# Revit family: 3M_Butterfly Valve_UNIVAL_BWN-0301 - 40-600 mm
name_source: partatom
category: Pipe Accessories
revit_build: Autodesk Revit 2016 (Build: 20150220_1215(x64)
units: mm (PartAtom-declared; Revit-internal decimal feet)

## family parameters
Always vertical = Yes
Cut with Voids When Loaded = No
OmniClass Number = 23.65.55.14.17
OmniClass Title = Adjusting/Controlling Valves for Liquid Services
Part Type = Valve - Breaks Into
Round Connector Dimension = Use Diameter
Shared = No
Work Plane-Based = No

## types (15) — shared parameters
Body Material = Cast iron
Certifications = TSE EAC CE
Connection Type = Wafer
Description = Wafer type butterfly valve
Description TR = Wafer tip kelebek vana
Disc Material = Nickel plated ductile iron
K Coefficient Table = Butterfly Valve Full Open
Loss Method = K Coefficient from Table
Manufacturer = Giacomini Unival
Giacomini Unival
Max. Working Pressure = 11 Bar
Max. Working Temperature = EPDM 120°C (water), NBR 90°C (water and petroleum oil)
Pressure Rating = PN16
Standard No = TS EN 593+A1
URL = http://www.unival.com.tr

## per-type parameters (varying)
- DN100: A=180 mm; B=100 mm; Body_r=73 mm; D=90 mm; DN=100 mm; Disc_r=50 mm  [stored 0.164042 ft]; E=52 mm; EarBottom_h=90 mm; EarEdge_r=25 mm  [stored 0.082021 ft]; Ear_x1=32 mm  [stored 0.104987 ft]; Ear_y1=40 mm  [stored 0.131234 ft]; Eclipse_angle=30.00°; Eclipse_h=86 mm; Eclipse_l=36 mm  [stored 0.11811 ft]; Eclipse_r1=26 mm  [stored 0.0853018 ft]; Eclipse_r2=20 mm  [stored 0.0656168 ft]; Gasket Material=EPDM / NBR; Kv=760; Max Diff. Pressure (Allowed)=3 Bar; Model=BWN-0201X100; Operator Type=M_Handle - Curved : Lever_260mm; Seat Material=EPDM / NBR / VITON / PTFE; Stem_D=35 mm  [stored 0.114829 ft]; Stem_top_h=1 mm  [stored 0.00328084 ft]; T=-10 mm  [stored -0.0328084 ft]
- DN250: A=274 mm; B=200 mm; Body_r=148 mm; D=125 mm; DN=250 mm; Disc_r=125 mm; E=69 mm; EarBottom_h=180 mm; EarEdge_r=32 mm  [stored 0.104987 ft]; Ear_x1=75 mm; Ear_y1=70 mm; Eclipse_angle=30.00°; Eclipse_h=168 mm; Eclipse_l=70 mm; Eclipse_r1=52 mm; Eclipse_r2=40 mm  [stored 0.131234 ft]; Gasket Material=EPDM, NBR; Kv=5050; Max Diff. Pressure (Allowed)=1.5 Bar; Model=BWN-0201X250; Operator Type=M_Handle - Curved : Lever_416mm; Seat Material=EPDM / NBR / VITON / PTFE; Stem_D=46 mm  [stored 0.150919 ft]; Stem_top_h=26 mm  [stored 0.0853018 ft]; T=-10 mm  [stored -0.0328084 ft]
- DN40: A=140 mm; B=64 mm; Body_r=43 mm  [stored 0.141076 ft]; D=90 mm; DN=40 mm; Disc_r=20 mm  [stored 0.0656168 ft]; E=35 mm  [stored 0.114829 ft]; EarBottom_h=54 mm  [stored 0.177165 ft]; EarEdge_r=10 mm  [stored 0.0328084 ft]; Ear_x1=20 mm  [stored 0.0656168 ft]; Ear_y1=22 mm  [stored 0.0721785 ft]; Eclipse_angle=20.00°; Eclipse_h=50 mm  [stored 0.164042 ft]; Eclipse_l=20 mm  [stored 0.0656168 ft]; Eclipse_r1=18 mm  [stored 0.0590551 ft]; Eclipse_r2=14 mm  [stored 0.0459318 ft]; Gasket Material=EPDM, NBR; Kv=49.5; Max Diff. Pressure (Allowed)=3 Bar; Model=BWN-0201X040; Operator Type=M_Handle - Curved : Lever_260mm; Seat Material=EPDM / NBR / VITON / PTFE; Stem_D=23 mm  [stored 0.0754593 ft]; Stem_top_h=1 mm  [stored 0.00328084 ft]; T=-10 mm  [stored -0.0328084 ft]
- DN50: A=140 mm; B=69 mm; Body_r=48 mm  [stored 0.15748 ft]; D=90 mm; DN=50 mm; Disc_r=25 mm  [stored 0.082021 ft]; E=43 mm  [stored 0.141076 ft]; EarBottom_h=60 mm; EarEdge_r=14 mm  [stored 0.0459318 ft]; Ear_x1=20 mm  [stored 0.0656168 ft]; Ear_y1=22 mm  [stored 0.0721785 ft]; Eclipse_angle=30.00°; Eclipse_h=56 mm  [stored 0.183727 ft]; Eclipse_l=22 mm  [stored 0.0721785 ft]; Eclipse_r1=18 mm  [stored 0.0590551 ft]; Eclipse_r2=14 mm  [stored 0.0459318 ft]; Gasket Material=EPDM, NBR; Kv=115; Max Diff. Pressure (Allowed)=3 Bar; Model=BWN-0201X050; Operator Type=M_Handle - Curved : Lever_260mm; Seat Material=EPDM / NBR / VITON / PTFE; Stem_D=29 mm; Stem_top_h=1 mm  [stored 0.00328084 ft]; T=-10 mm  [stored -0.0328084 ft]
- DN65: A=152 mm; B=76 mm; Body_r=56 mm  [stored 0.183727 ft]; D=90 mm; DN=65 mm; Disc_r=33 mm; E=45 mm  [stored 0.147638 ft]; EarBottom_h=70 mm; EarEdge_r=14 mm  [stored 0.0459318 ft]; Ear_x1=20 mm  [stored 0.0656168 ft]; Ear_y1=22 mm  [stored 0.0721785 ft]; Eclipse_angle=30.00°; Eclipse_h=65 mm; Eclipse_l=23 mm  [stored 0.0754593 ft]; Eclipse_r1=18 mm  [stored 0.0590551 ft]; Eclipse_r2=14 mm  [stored 0.0459318 ft]; Gasket Material=EPDM, NBR; Kv=255; Max Diff. Pressure (Allowed)=3 Bar; Model=BWN-0201X065; Operator Type=M_Handle - Curved : Lever_260mm; Seat Material=EPDM / NBR / VITON / PTFE; Stem_D=30 mm  [stored 0.0984252 ft]; Stem_top_h=1 mm  [stored 0.00328084 ft]; T=-10 mm  [stored -0.0328084 ft]
- DN80: A=160 mm; B=85 mm; Body_r=63 mm; D=90 mm; DN=80 mm; Disc_r=40 mm  [stored 0.131234 ft]; E=46 mm  [stored 0.150919 ft]; EarBottom_h=75 mm; EarEdge_r=20 mm  [stored 0.0656168 ft]; Ear_x1=22 mm  [stored 0.0721785 ft]; Ear_y1=22 mm  [stored 0.0721785 ft]; Eclipse_angle=30.00°; Eclipse_h=70 mm; Eclipse_l=27 mm  [stored 0.0885827 ft]; Eclipse_r1=20 mm  [stored 0.0656168 ft]; Eclipse_r2=15 mm  [stored 0.0492126 ft]; Gasket Material=EPDM, NBR; Kv=375; Max Diff. Pressure (Allowed)=3 Bar; Model=BWN-0201X080; Operator Type=M_Handle - Curved : Lever_260mm; Seat Material=EPDM / NBR / VITON / PTFE; Stem_D=31 mm; Stem_top_h=1 mm  [stored 0.00328084 ft]; T=-10 mm  [stored -0.0328084 ft]
- DN125: A=191 mm; B=120 mm; Body_r=86 mm; D=90 mm; DN=125 mm; Disc_r=63 mm; E=56 mm  [stored 0.183727 ft]; EarBottom_h=105 mm; EarEdge_r=28 mm  [stored 0.0918635 ft]; Ear_x1=34 mm; Ear_y1=36 mm  [stored 0.11811 ft]; Eclipse_angle=30.00°; Eclipse_h=98 mm; Eclipse_l=38 mm  [stored 0.124672 ft]; Eclipse_r1=28 mm  [stored 0.0918635 ft]; Eclipse_r2=22 mm  [stored 0.0721785 ft]; Gasket Material=EPDM, NBR; Kv=1030; Max Diff. Pressure (Allowed)=3 Bar; Model=BWN-0201X125; Operator Type=M_Handle - Curved : Lever_260mm; Seat Material=EPDM / NBR / VITON / PTFE; Stem_D=38 mm  [stored 0.124672 ft]; Stem_top_h=1 mm  [stored 0.00328084 ft]; T=-10 mm  [stored -0.0328084 ft]
- DN150: A=202 mm; B=132 mm; Body_r=98 mm; D=90 mm; DN=150 mm; Disc_r=75 mm; E=57 mm; EarBottom_h=117 mm; EarEdge_r=25 mm  [stored 0.082021 ft]; Ear_x1=42 mm  [stored 0.137795 ft]; Ear_y1=42 mm  [stored 0.137795 ft]; Eclipse_angle=30.00°; Eclipse_h=110 mm; Eclipse_l=46 mm  [stored 0.150919 ft]; Eclipse_r1=30 mm  [stored 0.0984252 ft]; Eclipse_r2=23 mm  [stored 0.0754593 ft]; Gasket Material=EPDM, NBR; Kv=1790; Max Diff. Pressure (Allowed)=3 Bar; Model=BWN-0201X150; Operator Type=M_Handle - Curved : Lever_260mm; Seat Material=EPDM / NBR / VITON / PTFE; Stem_D=38 mm  [stored 0.124672 ft]; Stem_top_h=1 mm  [stored 0.00328084 ft]; T=-10 mm  [stored -0.0328084 ft]
- DN200: A=237 mm; B=160 mm; Body_r=123 mm; D=125 mm; DN=200 mm; Disc_r=100 mm; E=60 mm; EarBottom_h=145 mm; EarEdge_r=30 mm  [stored 0.0984252 ft]; Ear_x1=56 mm  [stored 0.183727 ft]; Ear_y1=52 mm; Eclipse_angle=30.00°; Eclipse_h=136 mm; Eclipse_l=58 mm; Eclipse_r1=42 mm  [stored 0.137795 ft]; Eclipse_r2=32 mm  [stored 0.104987 ft]; Gasket Material=EPDM, NBR; Kv=3450; Max Diff. Pressure (Allowed)=3 Bar; Model=BWN-0201X200; Operator Type=M_Handle - Curved : Lever_326mm; Seat Material=EPDM / NBR / VITON / PTFE; Stem_D=40 mm  [stored 0.131234 ft]; Stem_top_h=23 mm  [stored 0.0754593 ft]; T=-10 mm  [stored -0.0328084 ft]
- DN300: A=312 mm; B=230 mm; Body_r=173 mm; D=125 mm; DN=300 mm; Disc_r=150 mm; E=80 mm; EarBottom_h=208 mm; EarEdge_r=40 mm  [stored 0.131234 ft]; Ear_x1=80 mm; Ear_y1=80 mm; Eclipse_angle=30.00°; Eclipse_h=194 mm; Eclipse_l=84 mm; Eclipse_r1=58 mm; Eclipse_r2=45 mm  [stored 0.147638 ft]; Gasket Material=EPDM, NBR; Kv=7420; Max Diff. Pressure (Allowed)=1.5 Bar; Model=BWN-0201X300; Operator Type=M_Handle - Curved : Lever_416mm; Seat Material=EPDM / NBR / VITON / PTFE; Stem_D=53 mm  [stored 0.173885 ft]; Stem_top_h=26 mm  [stored 0.0853018 ft]; T=-10 mm  [stored -0.0328084 ft]
- DN350: A=368 mm; B=280 mm; Body_r=198 mm; D=125 mm; DN=350 mm; Disc_r=175 mm; E=78 mm; EarBottom_h=270 mm; EarEdge_r=44 mm  [stored 0.144357 ft]; Ear_x1=86 mm; Ear_y1=90 mm; Eclipse_angle=30.00°; Eclipse_h=228 mm; Eclipse_l=78 mm; Eclipse_r1=70 mm; Eclipse_r2=54 mm  [stored 0.177165 ft]; Gasket Material=EPDM, NBR; Kv=10300; Model=BWN-0201X350; Operator Type=M_Gear - Operator  : GearS; Seat Material=EPDM / NBR / VITON; Stem_D=52 mm; Stem_top_h=1 mm  [stored 0.00328084 ft]; T=-24 mm  [stored -0.0787402 ft]
- DN400: A=400 mm; B=310 mm; Body_r=223 mm; D=175 mm; DN=400 mm; Disc_r=200 mm; E=88 mm; EarBottom_h=300 mm; EarEdge_r=44 mm  [stored 0.144357 ft]; Ear_x1=94 mm; Ear_y1=90 mm; Eclipse_angle=30.00°; Eclipse_h=256 mm; Eclipse_l=84 mm; Eclipse_r1=74 mm; Eclipse_r2=57 mm; Gasket Material=EPDM, NBR; Kv=14007; Model=BWN-0201X400; Operator Type=M_Gear - Operator  : GearM; Seat Material=EPDM / NBR / VITON; Stem_D=59 mm; Stem_top_h=1 mm  [stored 0.00328084 ft]; T=-25 mm  [stored -0.082021 ft]
- DN450: A=422 mm; B=340 mm; Body_r=248 mm; D=175 mm; DN=450 mm; Disc_r=225 mm; E=109 mm; EarBottom_h=330 mm; EarEdge_r=44 mm  [stored 0.144357 ft]; Ear_x1=94 mm; Ear_y1=90 mm; Eclipse_angle=30.00°; Eclipse_h=280 mm; Eclipse_l=86 mm; Eclipse_r1=74 mm; Eclipse_r2=57 mm; Gasket Material=EPDM, NBR; Kv=18551; Model=BWN-0201X450; Operator Type=M_Gear - Operator  : GearM; Seat Material=EPDM / NBR / VITON; Stem_D=73 mm; Stem_top_h=1 mm  [stored 0.00328084 ft]; T=-26 mm
- DN500: A=480 mm; B=388 mm; Body_r=273 mm; D=210 mm; DN=500 mm; Disc_r=250 mm; E=127 mm; EarBottom_h=370 mm; EarEdge_r=50 mm  [stored 0.164042 ft]; Ear_x1=110 mm; Ear_y1=96 mm; Eclipse_angle=30.00°; Eclipse_h=310 mm; Eclipse_l=100 mm; Eclipse_r1=84 mm; Eclipse_r2=65 mm; Gasket Material=EPDM, NBR; Kv=23853; Model=BWN-0201X500; Operator Type=M_Gear - Operator  : GearL; Seat Material=EPDM / NBR / VITON; Stem_D=85 mm; Stem_top_h=1 mm  [stored 0.00328084 ft]; T=-25 mm  [stored -0.082021 ft]
- DN600: A=562 mm; B=450 mm; Body_r=323 mm; D=210 mm; DN=600 mm; Disc_r=300 mm; E=154 mm; EarBottom_h=436 mm; EarEdge_r=50 mm  [stored 0.164042 ft]; Ear_x1=130 mm; Ear_y1=130 mm; Eclipse_angle=30.00°; Eclipse_h=376 mm; Eclipse_l=116 mm; Eclipse_r1=100 mm; Eclipse_r2=77 mm; Gasket Material=EPDM, NBR; Kv=36894; Model=BWN-0201X600; Operator Type=M_Gear - Operator  : GearL; Seat Material=EPDM / NBR / VITON; Stem_D=103 mm; Stem_top_h=1 mm  [stored 0.00328084 ft]; T=-30 mm  [stored -0.0984252 ft]

note: [stored X ft] marks values corroborated as IEEE doubles in the binary element streams (Revit-internal decimal feet)

## geometry (parser evidence)
native form markers: Sweep x8
no freeform markers — native parametric forms only
